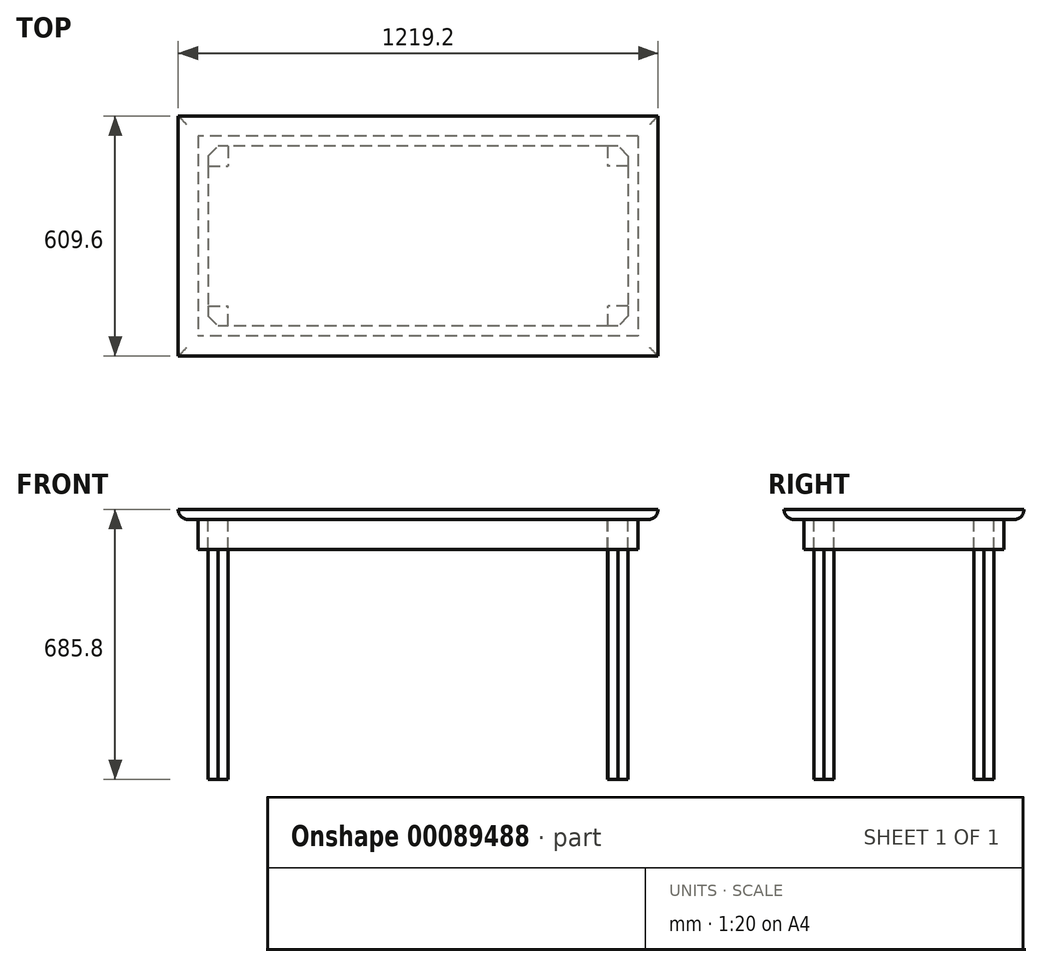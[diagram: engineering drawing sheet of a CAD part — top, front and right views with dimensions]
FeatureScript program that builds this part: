
annotation { "Feature Type Name" : "Feature", "Feature Type Description" : "" }
export const myFeature = defineFeature(function(context is Context, id is Id, definition is map)
    precondition{}
    {
        {
            var Q0;
            Q0=qCreatedBy(makeId("Top.planeOp"),FACE);
            var sketch = newSketch(context, id + "F0", { "sketchPlane" : qUnion([Q0])});
            skLineSegment(sketch, "E0.bottom", {"start": v(609.6, -304.8) * mm, "end": v(-609.6, -304.8) * mm});
            skLineSegment(sketch, "E0.top", {"start": v(609.6, 304.8) * mm, "end": v(-609.6, 304.8) * mm});
            skLineSegment(sketch, "E0.left", {"start": v(609.6, -304.8) * mm, "end": v(609.6, 304.8) * mm});
            skLineSegment(sketch, "E0.right", {"start": v(-609.6, -304.8) * mm, "end": v(-609.6, 304.8) * mm});
            skPoint(sketch, "E0.middle", {"position": v(0, 0) * mm});
            skSolve(sketch);
        }
        {
            var Q0;
            Q0=makeQuery(id+"F0.imprint","IMPRINT",FACE,{"disambiguationData":[TD([[makeQuery(id+"F0.imprint","IMPRINT",EDGE,{"derivedFrom":sQuery(id+"F0.wireOp",EDGE,"E0.bottom")}),-1.0]])]});
            extrude(context, id + "F1", {"entities" : qUnion([Q0]), "depth" : 25.4 * mm});
        }
        {
            var Q0;
            Q0=makeQuery(id+"F1.opExtrude","CAP_FACE",FACE,{"disambiguationData":[OSD([sQuery(id+"F0.wireOp",EDGE,"E0.bottom"),sQuery(id+"F0.wireOp",EDGE,"E0.top"),sQuery(id+"F0.wireOp",EDGE,"E0.left"),sQuery(id+"F0.wireOp",EDGE,"E0.right")])],"isStart":true});
            var sketch = newSketch(context, id + "F2", { "sketchPlane" : qUnion([Q0])});
            skLineSegment(sketch, "E1.bottom", {"start": v(558.8, -254) * mm, "end": v(-558.8, -254) * mm});
            skLineSegment(sketch, "E1.top", {"start": v(558.8, 254) * mm, "end": v(-558.8, 254) * mm});
            skLineSegment(sketch, "E1.left", {"start": v(558.8, -254) * mm, "end": v(558.8, 254) * mm});
            skLineSegment(sketch, "E1.right", {"start": v(-558.8, -254) * mm, "end": v(-558.8, 254) * mm});
            skPoint(sketch, "E1.middle", {"position": v(0, 0) * mm});
            skLineSegment(sketch, "E2.bottom", {"start": v(533.4, -228.6) * mm, "end": v(-533.4, -228.6) * mm});
            skLineSegment(sketch, "E2.top", {"start": v(533.4, 228.6) * mm, "end": v(-533.4, 228.6) * mm});
            skLineSegment(sketch, "E2.left", {"start": v(533.4, -228.6) * mm, "end": v(533.4, 228.6) * mm});
            skLineSegment(sketch, "E2.right", {"start": v(-533.4, -228.6) * mm, "end": v(-533.4, 228.6) * mm});
            skSolve(sketch);
        }
        {
            var Q0;
            Q0=makeQuery(id+"F2.imprint","IMPRINT",FACE,{"disambiguationData":[TD([[makeQuery(id+"F2.imprint","IMPRINT",EDGE,{"derivedFrom":sQuery(id+"F2.wireOp",EDGE,"E1.bottom")}),-1.0]])]});
            extrude(context, id + "F3", {"entities" : qUnion([Q0]), "operationType" : NewBodyOperationType.ADD, "depth" : 76.2 * mm});
        }
        {
            var Q0;
            Q0=makeQuery(id+"F3.boolean.opBoolean","SPLIT",FACE,{"disambiguationData":[TD([makeQuery(id+"F3.opExtrude","SWEPT_FACE",FACE,{"disambiguationData":[OSD([sQuery(id+"F2.wireOp",EDGE,"E2.bottom")])]})])],"derivedFrom":makeQuery(id+"F1.opExtrude","CAP_FACE",FACE,{"disambiguationData":[OSD([sQuery(id+"F0.wireOp",EDGE,"E0.bottom"),sQuery(id+"F0.wireOp",EDGE,"E0.top"),sQuery(id+"F0.wireOp",EDGE,"E0.left"),sQuery(id+"F0.wireOp",EDGE,"E0.right")])],"isStart":true})});
            var sketch = newSketch(context, id + "F4", { "sketchPlane" : qUnion([Q0])});
            skLineSegment(sketch, "E3.bottom", {"start": v(-533.4, -228.6) * mm, "end": v(-482.6, -228.6) * mm});
            skLineSegment(sketch, "E3.top", {"start": v(-533.4, -177.8) * mm, "end": v(-482.6, -177.8) * mm});
            skLineSegment(sketch, "E3.left", {"start": v(-533.4, -228.6) * mm, "end": v(-533.4, -177.8) * mm});
            skLineSegment(sketch, "E3.right", {"start": v(-482.6, -228.6) * mm, "end": v(-482.6, -177.8) * mm});
            skLineSegment(sketch, "E4.bottom", {"start": v(533.4, 228.6) * mm, "end": v(482.6, 228.6) * mm});
            skLineSegment(sketch, "E4.top", {"start": v(533.4, 177.8) * mm, "end": v(482.6, 177.8) * mm});
            skLineSegment(sketch, "E4.left", {"start": v(533.4, 228.6) * mm, "end": v(533.4, 177.8) * mm});
            skLineSegment(sketch, "E4.right", {"start": v(482.6, 228.6) * mm, "end": v(482.6, 177.8) * mm});
            skLineSegment(sketch, "E5.bottom", {"start": v(533.4, -228.6) * mm, "end": v(480.5, -228.6) * mm});
            skLineSegment(sketch, "E5.top", {"start": v(533.4, -177.8) * mm, "end": v(480.5, -177.8) * mm});
            skLineSegment(sketch, "E5.left", {"start": v(533.4, -228.6) * mm, "end": v(533.4, -177.8) * mm});
            skLineSegment(sketch, "E5.right", {"start": v(480.5, -228.6) * mm, "end": v(480.5, -177.8) * mm});
            skLineSegment(sketch, "E6.bottom", {"start": v(-533.4, 228.6) * mm, "end": v(-482.6, 228.6) * mm});
            skLineSegment(sketch, "E6.top", {"start": v(-533.4, 177.8) * mm, "end": v(-482.6, 177.8) * mm});
            skLineSegment(sketch, "E6.left", {"start": v(-533.4, 228.6) * mm, "end": v(-533.4, 177.8) * mm});
            skLineSegment(sketch, "E6.right", {"start": v(-482.6, 228.6) * mm, "end": v(-482.6, 177.8) * mm});
            skSolve(sketch);
        }
        {
            var Q0;
            Q0=makeQuery(id+"F4.imprint","IMPRINT",FACE,{"disambiguationData":[TD([[makeQuery(id+"F4.imprint","IMPRINT",EDGE,{"derivedFrom":sQuery(id+"F4.wireOp",EDGE,"E6.bottom")}),1.0]])]});
            var Q1;
            Q1=makeQuery(id+"F4.imprint","IMPRINT",FACE,{"disambiguationData":[TD([[makeQuery(id+"F4.imprint","IMPRINT",EDGE,{"derivedFrom":sQuery(id+"F4.wireOp",EDGE,"E3.bottom")}),-1.0]])]});
            var Q2;
            Q2=makeQuery(id+"F4.imprint","IMPRINT",FACE,{"disambiguationData":[TD([[makeQuery(id+"F4.imprint","IMPRINT",EDGE,{"derivedFrom":sQuery(id+"F4.wireOp",EDGE,"E5.bottom")}),-1.0]])]});
            var Q3;
            Q3=makeQuery(id+"F4.imprint","IMPRINT",FACE,{"disambiguationData":[TD([[makeQuery(id+"F4.imprint","IMPRINT",EDGE,{"derivedFrom":sQuery(id+"F4.wireOp",EDGE,"E4.bottom")}),1.0]])]});
            extrude(context, id + "F5", {"entities" : qUnion([Q0, Q1, Q2, Q3]), "operationType" : NewBodyOperationType.ADD, "depth" : 660.4 * mm});
        }
        {
            var Q0;
            Q0=makeQuery(id+"F1.opExtrude","CAP_EDGE",EDGE,{"disambiguationData":[OSD([sQuery(id+"F0.wireOp",EDGE,"E0.top")])],"isStart":true});
            var Q1;
            Q1=makeQuery(id+"F1.opExtrude","CAP_EDGE",EDGE,{"disambiguationData":[OSD([sQuery(id+"F0.wireOp",EDGE,"E0.right")])],"isStart":true});
            var Q2;
            Q2=makeQuery(id+"F1.opExtrude","CAP_EDGE",EDGE,{"disambiguationData":[OSD([sQuery(id+"F0.wireOp",EDGE,"E0.left")])],"isStart":true});
            var Q3;
            Q3=makeQuery(id+"F1.opExtrude","CAP_EDGE",EDGE,{"disambiguationData":[OSD([sQuery(id+"F0.wireOp",EDGE,"E0.bottom")])],"isStart":true});
            fillet(context, id + "F6", {"entities" : qUnion([Q0, Q1, Q2, Q3]), "radius" : 25.4 * mm, "tangentPropagation" : true, "allowEdgeOverflow" : false});
        }
        {
            var Q0;
            Q0=makeQuery(id+"F5.opExtrude","SWEPT_EDGE",EDGE,{"disambiguationData":[OSD([sQuery(id+"F4.wireOp",EDGE,"E6.bottom"),sQuery(id+"F4.wireOp",EDGE,"E6.left")])]});
            var Q1;
            Q1=makeQuery(id+"F5.opExtrude","SWEPT_EDGE",EDGE,{"disambiguationData":[OSD([sQuery(id+"F4.wireOp",EDGE,"E3.bottom"),sQuery(id+"F4.wireOp",EDGE,"E3.left")])]});
            var Q2;
            Q2=makeQuery(id+"F5.opExtrude","SWEPT_EDGE",EDGE,{"disambiguationData":[OSD([sQuery(id+"F4.wireOp",EDGE,"E5.bottom"),sQuery(id+"F4.wireOp",EDGE,"E5.left")])]});
            var Q3;
            Q3=makeQuery(id+"F5.opExtrude","SWEPT_EDGE",EDGE,{"disambiguationData":[OSD([sQuery(id+"F4.wireOp",EDGE,"E4.bottom"),sQuery(id+"F4.wireOp",EDGE,"E4.left")])]});
            chamfer(context, id + "F7", {"entities" : qUnion([Q0, Q1, Q2, Q3]), "width" : 25.4 * mm, "tangentPropagation" : true});
        }
    });
